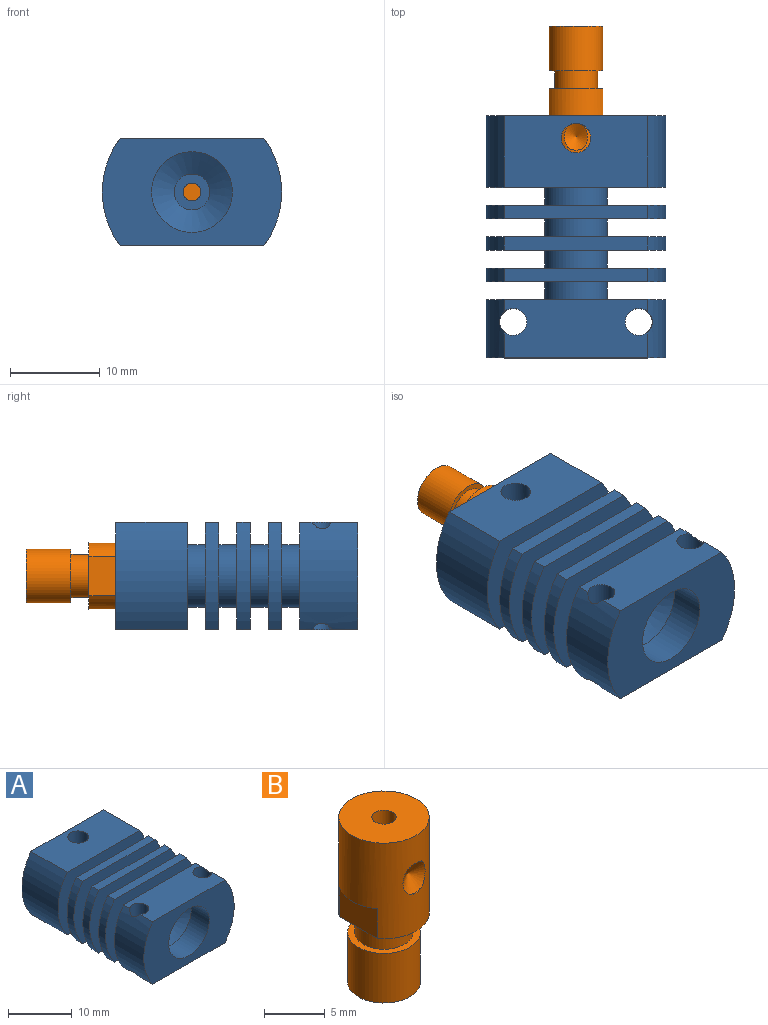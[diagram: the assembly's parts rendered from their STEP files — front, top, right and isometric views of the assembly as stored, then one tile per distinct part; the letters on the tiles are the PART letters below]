
ASSEMBLY  parts=2 mates=1
PART A: 48 faces, bbox 20x27x12 mm
  f0: cylinder r=2mm len=4mm, axis (0,-1,0), area 18.8mm2, adj f45,f46
  f1: cylinder r=1mm len=13.35mm, axis (0,1,0), area 83.9mm2, adj f43,f45
  f2: plane 16x6.5mm, normal (0,0,1), area 91.4mm2, adj f7,f8,f9,f33,f36,f37
  f3: cylinder r=10mm len=12mm, axis (0,1,0), area 103mm2, adj f5,f6,f10,f13
  f4: cylinder r=10mm len=12mm, axis (0,1,0), area 103mm2, adj f5,f6,f10,f13
  f5: plane 16x8mm, normal (0,0,-1), area 128mm2, adj f3,f4,f10,f13
  f6: plane 16x8mm, normal (0,0,1), area 119.4mm2, adj f3,f4,f10,f13,f38
  f7: cylinder r=10mm len=12mm, axis (0,1,0), area 80.9mm2, adj f2,f9,f11,f33,f36
  f8: cylinder r=10mm len=12mm, axis (0,1,0), area 80.9mm2, adj f2,f9,f11,f33,f37
  f9: plane 20x12mm, normal (0,-1,0), area 161.1mm2, adj f2,f7,f8,f11,f47
  f10: plane 20x12mm, normal (0,1,0), area 170.7mm2, adj f3,f4,f5,f6,f40,f42,f44
  f11: plane 16x6.5mm, normal (0,0,-1), area 91.4mm2, adj f7,f8,f9,f33,f36,f37
  f12: plane 20x12mm, normal (0,1,0), area 186.2mm2, adj f14,f15,f16,f17,f18
  f13: plane 20x12mm, normal (0,-1,0), area 185.1mm2, adj f3,f4,f5,f6,f14,f39,f41
  f14: cylinder r=3.5mm len=7mm, axis (0,1,0), area 44mm2, adj f12,f13
  f15: plane 16x1.5mm, normal (0,0,1), area 24mm2, adj f12,f17,f18,f20
  f16: plane 16x1.5mm, normal (0,0,-1), area 24mm2, adj f12,f17,f18,f20
  f17: cylinder r=10mm len=12mm, axis (0,1,0), area 19.3mm2, adj f12,f15,f16,f20
  f18: cylinder r=10mm len=12mm, axis (0,1,0), area 19.3mm2, adj f12,f15,f16,f20
  f19: plane 20x12mm, normal (0,1,0), area 186.2mm2, adj f21,f22,f23,f24,f25
  f20: plane 20x12mm, normal (0,-1,0), area 186.2mm2, adj f15,f16,f17,f18,f21
  f21: cylinder r=3.5mm len=7mm, axis (0,1,0), area 44mm2, adj f19,f20
  f22: plane 16x1.5mm, normal (0,0,1), area 24mm2, adj f19,f24,f25,f27
  f23: plane 16x1.5mm, normal (0,0,-1), area 24mm2, adj f19,f24,f25,f27
  f24: cylinder r=10mm len=12mm, axis (0,1,0), area 19.3mm2, adj f19,f22,f23,f27
  f25: cylinder r=10mm len=12mm, axis (0,1,0), area 19.3mm2, adj f19,f22,f23,f27
  f26: plane 20x12mm, normal (0,1,0), area 186.2mm2, adj f28,f29,f30,f31,f32
  f27: plane 20x12mm, normal (0,-1,0), area 186.2mm2, adj f22,f23,f24,f25,f28
  f28: cylinder r=3.5mm len=7mm, axis (0,1,0), area 44mm2, adj f26,f27
  f29: plane 16x1.5mm, normal (0,0,1), area 24mm2, adj f26,f31,f32,f34
  f30: plane 16x1.5mm, normal (0,0,-1), area 24mm2, adj f26,f31,f32,f34
  f31: cylinder r=10mm len=12mm, axis (0,1,0), area 19.3mm2, adj f26,f29,f30,f34
  f32: cylinder r=10mm len=12mm, axis (0,1,0), area 19.3mm2, adj f26,f29,f30,f34
  f33: plane 20x12mm, normal (0,1,0), area 186.2mm2, adj f2,f7,f8,f11,f35
  f34: plane 20x12mm, normal (0,-1,0), area 186.2mm2, adj f29,f30,f31,f32,f35
  f35: cylinder r=3.5mm len=7mm, axis (0,1,0), area 44mm2, adj f33,f34
  f36: cylinder r=1.5mm len=12mm, axis (0,0,1), area 110.7mm2, adj f2,f7,f11
  f37: cylinder r=1.5mm len=12mm, axis (0,0,1), area 110.7mm2, adj f2,f8,f11
  f38: cylinder r=1.65mm len=3.3mm, axis (0,0,1), area 25.3mm2, adj f6,f44
  f39: cone r=0mm half-angle=59deg, axis (0,1,0), area 5.1mm2, adj f13,f40
  f40: cylinder r=1.25mm len=7.5mm, axis (0,1,0), area 58.9mm2, adj f10,f39
  f41: cone r=0mm half-angle=59deg, axis (0,1,0), area 5.1mm2, adj f13,f42
  f42: cylinder r=1.25mm len=7.5mm, axis (0,1,0), area 58.9mm2, adj f10,f41
  f43: plane 7.5x7.5mm, normal (0,1,0), area 41mm2, adj f1,f44
  f44: cylinder r=3.75mm len=7.5mm, axis (0,1,0), area 147.9mm2, adj f10,f38,f43
  f45: plane 4x4mm, normal (0,-1,0), area 9.4mm2, adj f0,f1
  f46: cone r=0mm half-angle=59deg, axis (0,-1,0), area 59.6mm2, adj f0,f47
  f47: cylinder r=4.5mm len=9mm, axis (0,-1,0), area 113.1mm2, adj f9,f46
PART B: 18 faces, bbox 7.5x7.5x16.6 mm
  f0: cylinder r=1mm len=6.64mm, axis (0,0,1), area 41.7mm2, adj f3,f8
  f1: plane 4.42x0.73mm, normal (0,0,-1), area 2.2mm2, adj f2,f9
  f2: cylinder r=3.73mm len=9.64mm, axis (0,0,-1), area 190.8mm2, adj f1,f3,f4,f5,f6,f7,f9,f10
  f3: plane 7.45x7.45mm, normal (0,0,1), area 40.4mm2, adj f0,f2
  f4: plane 4.42x0.73mm, normal (0,0,-1), area 2.2mm2, adj f2,f10
  f5: cone r=0mm half-angle=59deg, axis (0,-1,0), area 7.4mm2, adj f2,f6,f7
  f6: cylinder r=1.5mm len=1.71mm, axis (0,-1,0), area 0.1mm2, adj f2,f5
  f7: cylinder r=1.5mm len=1.71mm, axis (0,-1,0), area 0.1mm2, adj f2,f5
  f8: plane 2x2mm, normal (0,0,1), area 3.1mm2, adj f0
  f9: plane 4.42x3mm, normal (-1,0,0), area 13.2mm2, adj f1,f2,f11
  f10: plane 4.42x3mm, normal (1,0,0), area 13.2mm2, adj f2,f4,f11
  f11: plane 7.45x6mm, normal (0,0,-1), area 21.1mm2, adj f2,f9,f10,f12
  f12: cylinder r=2.4mm len=4.8mm, axis (0,0,1), area 30.2mm2, adj f11,f15
  f13: cylinder r=3mm len=6mm, axis (0,0,1), area 94.2mm2, adj f14,f15
  f14: plane 6x6mm, normal (0,0,-1), area 25.1mm2, adj f13,f17
  f15: plane 6x6mm, normal (0,0,1), area 10.2mm2, adj f12,f13
  f16: plane 2x2mm, normal (0,0,-1), area 3.1mm2, adj f17
  f17: cylinder r=1mm len=7.99mm, axis (0,0,1), area 50.2mm2, adj f14,f16
PLACE A t=(0.28,13.43,-0.28)mm fixed
PLACE B rot(axis=(0,-0.71,0.71),180deg) t=(0.28,20.43,-0.28)mm
MATE fastened B.f2 <-> A.f44  axis (0,-1,0) through (0.28,6.78,-0.28)mm
